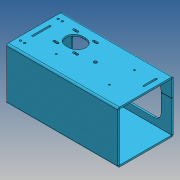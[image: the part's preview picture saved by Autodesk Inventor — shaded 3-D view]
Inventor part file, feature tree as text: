
AUTODESK INVENTOR PART (.ipt)
format: ipt  version: 2017 (Build 210142000, 142)  size: 389,120 bytes
history: native  units: mm
features: other x15, sketch x5, extrude x2, projected_geometry x1
ambient origin geometry x8: Origin, YZ Plane, XZ Plane, XY Plane, X Axis, Y Axis, Z Axis, Center Point
bodies: Body1 (feature_tree)
feature tree (23):
  other  "Sólido1"
  extrude  "Extrusión1"  Depth=56.4mm
  other  "Pestaña1"
  sketch  "Boceto4"  dims[d6=8.0mm]
  other  "Cara1"
  other  "Cara2"
  other  "Cara3"
  extrude  "Extrusión2"  Depth=67.5mm
  sketch  "Boceto1"  dims[d0=6.35mm d1=56.4mm]
  sketch  "Boceto2"  dims[d2=67.5mm d4=200.0mm]
  other  "Placa1"
  other  "Doblez1"
  other  "Esquina1"
  sketch  "Boceto3"  dims[d5=42.0mm]
  projected_geometry  "Contorno proyectado1"
  other  "Placa2"
  other  "Doblez2"
  other  "Placa3"
  other  "Doblez3"
  sketch  "Boceto5"  dims[d7=11.235mm d8=5.0mm d9=39.14mm d10=8.0mm d11=55.14mm d12=8.0mm d13=4.0mm d14=115.0mm d15=25.0mm d16=60.0mm d17=60.0mm d18=4.0mm d19=20.0mm d20=22.0mm d21=128.27mm d22=50.0mm d23=25.0mm d24=4.0mm d25=0.0mm d26=4.0mm d27=2.0mm d28=8.0mm d29=4.0mm d30=120.0mm d31=90.0deg d32=0.1mm d33=16.0mm d34=4.0mm d35=4.0mm d36=4.0mm d37=8.0mm d38=25.0mm d39=25.0mm d40=4.0mm d41=0.0mm d42=47.14mm d43=47.14mm d44=20.0mm d45=8.0mm d46=8.0mm d47=15.0mm d48=0.1mm d49=4.0mm d50=2.0mm d51=8.0mm d52=4.0mm d53=0.1mm d54=4.0mm d55=2.0mm d56=8.0mm d57=4.0mm d58=0.5mm d59=0.5mm d60=20.0mm d61=20.0mm d62=4.0mm d63=41.0mm d64=12.5mm d65=5.0mm d66=10.0mm d67=7.0mm d68=45.0mm d69=12.5mm d70=4.0mm d71=25.0mm d72=25.0mm d73=0.1mm d74=4.0mm d75=2.0mm d76=8.0mm d77=4.0mm d78=4.0mm d79=41.0mm d80=39.833333mm d81=79.666667mm d82=84.0mm d83=5.0mm]
  other  "Placa4"
  other  "Doblez4"
  other  "Definición1"
